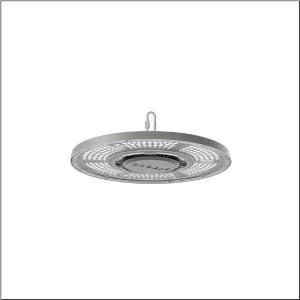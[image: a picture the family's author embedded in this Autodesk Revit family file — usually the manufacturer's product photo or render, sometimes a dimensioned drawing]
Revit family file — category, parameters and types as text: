
# Revit family: highbay_31-s_51hc42da4fmb
name_source: partatom
category: Lighting Fixtures
units: mm (PartAtom-declared; Revit-internal decimal feet)

## family parameters
Cut with Voids When Loaded = No
Host = Face
Light Source = No
Part Type = Normal
Room Calculation Point = No
Round Connector Dimension = Use Diameter
Shared = No

## types (1)
- Highbay 31-S (1 x LED, 14000 lm, 94 W, 4000K)
    Apparent Load = 94 VA
    CIE Flux Codes = 77 99 100 100 100
    Color Rendering = 80
    Color Temperature = 4000K
    Default Elevation = 1800 mm
    Description = Highbay 31-S, LED high bay luminaire, primary light control with lens, of PC, primary optical cover: cover panel, of PC, transparent, light emission: direct distribution, primary light characteristic: rotationally symmetric, installation type: suspended mounting, surface-mounted, LED, rated luminous flux: 14.000lm, luminous efficacy: 150lm/W, light colour: 840, colour temperature: 4000K, control gear: ECG DALI, with cable, 5x 1.0mm², free wire ends, mains connection: 220..240V, AC/DC, 0/50..60Hz, cable length: 1,5m, rated input power: 94W, housing, rotationally symmetric, of diecast aluminium, powder-coated, grey aluminium (RAL 9007), with hook on luminaire side, incl. screw, diameter: 339mm, protection rating (complete): IP65, insulation class (complete): insulation class I (protective earthing), certification: CE, ENEC, UKCA, protection symbol: D, impact resistance: IK08, permissible operating ambient temperature: -30..+45°C, standard: EN 60598-2-22, EN 60598, corresponds to IFS (International Featured Standards) requirements for safety and quality in the food industry, packaging unit: 1 piece
    Height = 141 mm
    Lamp = 1 x LED
    Lamp Light Flux = 14000 lm
    Lamp Power = 94 W
    Lamp count = 1
    Length = 339 mm
    Luminous efficacy = 149 lm/W
    Manufacturer = Siteco
    ModVariant = No
    Model = 51HC42DA4FMB
    Mounting Place = Ceiling
    Mounting Type = Pendant
    Number of Poles = 1
    OnlyDefault = Yes
    Power Factor = 1
    Product Name = Highbay 31-S
    Product group = LED high bay luminaire
    ProductGroupID = 903
    Protection Class = Protection class I
    Protection Degree = IP 65
    RLX_Detail_Level = 1
    RLX_Emergency_Light_Flux = 0 lm
    RLX_Emergency_Type = 0
    RLX_Emergency_Type_DB = No
    RlxData = <blob elided: 162189 chars, md5=e0103c02>
    Socket = socket
    Standby Power = 0 W
    System Light Flux = 14000 lm
    System Power = 94 W
    Type Comments = Product without accessories
    Type Image = l_1007237.jpg
    URL = http://relux.com
    VarID = ---
    Voltage = 0 V
    Weight = 0.00 kg
    Width = 0 mm  [stored 0 ft]

note: [stored X ft] marks values corroborated as IEEE doubles in the binary element streams (Revit-internal decimal feet)

## geometry (parser evidence)
native form markers: Blend x4, Sweep x8
no freeform markers — native parametric forms only
